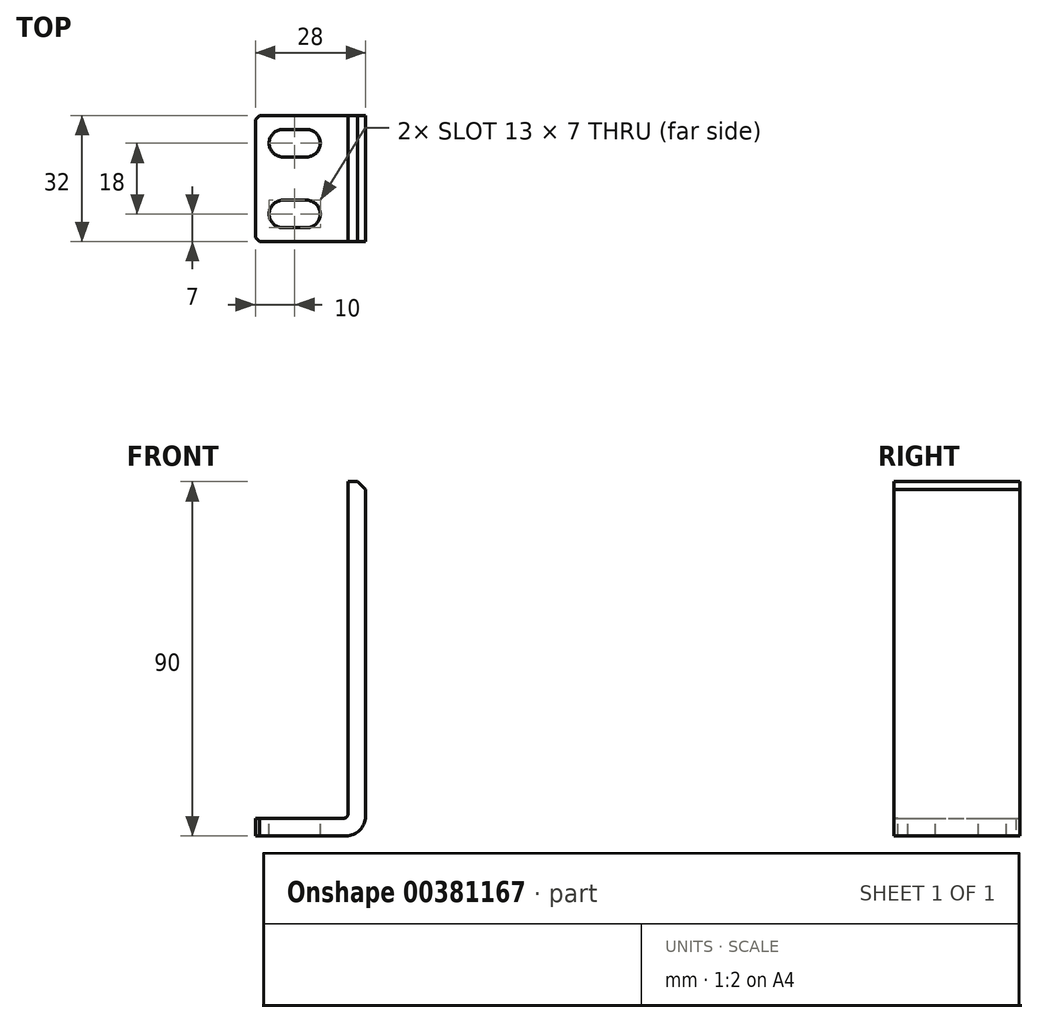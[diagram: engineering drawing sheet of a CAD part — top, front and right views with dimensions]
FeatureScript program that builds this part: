
annotation { "Feature Type Name" : "Feature", "Feature Type Description" : "" }
export const myFeature = defineFeature(function(context is Context, id is Id, definition is map)
    precondition{}
    {
        {
            var Q0;
            Q0=qCreatedBy(makeId("Front.planeOp"),FACE);
            var sketch = newSketch(context, id + "F0", { "sketchPlane" : qUnion([Q0])});
            skLineSegment(sketch, "E0.bottom", {"start": v(0, 90) * mm, "end": v(-4.5, 90) * mm});
            skLineSegment(sketch, "E0.top", {"start": v(0, 0) * mm, "end": v(-28, 0) * mm});
            skLineSegment(sketch, "E0.left", {"start": v(0, 90) * mm, "end": v(0, 0) * mm});
            skLineSegment(sketch, "E0.right", {"start": v(-28, 4.5) * mm, "end": v(-28, 0) * mm});
            skLineSegment(sketch, "E1", {"start": v(-4.5, 90) * mm, "end": v(-4.5, 4.5) * mm});
            skLineSegment(sketch, "E2", {"start": v(-28, 4.5) * mm, "end": v(-4.5, 4.5) * mm});
            skSolve(sketch);
        }
        {
            var Q0;
            Q0=makeQuery(id+"F0.imprint","IMPRINT",FACE,{"disambiguationData":[TD([[makeQuery(id+"F0.imprint","IMPRINT",EDGE,{"derivedFrom":sQuery(id+"F0.wireOp",EDGE,"E0.bottom")}),1.0]])]});
            extrude(context, id + "F1", {"entities" : qUnion([Q0]), "depth" : 32 * mm});
        }
        {
            var Q0;
            Q0=makeQuery(id+"F1.opExtrude","SWEPT_EDGE",EDGE,{"disambiguationData":[OSD([sQuery(id+"F0.wireOp",EDGE,"E1"),sQuery(id+"F0.wireOp",EDGE,"E2")])]});
            fillet(context, id + "F2", {"entities" : qUnion([Q0]), "radius" : 1 * mm, "tangentPropagation" : true, "allowEdgeOverflow" : false});
        }
        {
            var Q0;
            Q0=makeQuery(id+"F1.opExtrude","SWEPT_EDGE",EDGE,{"disambiguationData":[OSD([sQuery(id+"F0.wireOp",EDGE,"E0.top"),sQuery(id+"F0.wireOp",EDGE,"E0.left")])]});
            fillet(context, id + "F3", {"entities" : qUnion([Q0]), "radius" : 5 * mm, "tangentPropagation" : true, "allowEdgeOverflow" : false});
        }
        {
            var Q0;
            Q0=makeQuery(id+"F1.opExtrude","SWEPT_EDGE",EDGE,{"disambiguationData":[OSD([sQuery(id+"F0.wireOp",EDGE,"E0.bottom"),sQuery(id+"F0.wireOp",EDGE,"E0.left")])]});
            chamfer(context, id + "F4", {"entities" : qUnion([Q0]), "width" : 2 * mm, "tangentPropagation" : true});
        }
        {
            var Q0;
            Q0=makeQuery(id+"F1.opExtrude","CAP_EDGE",EDGE,{"disambiguationData":[OSD([sQuery(id+"F0.wireOp",EDGE,"E0.right")])],"isStart":false});
            var Q1;
            Q1=makeQuery(id+"F1.opExtrude","CAP_EDGE",EDGE,{"disambiguationData":[OSD([sQuery(id+"F0.wireOp",EDGE,"E0.right")])],"isStart":true});
            chamfer(context, id + "F5", {"entities" : qUnion([Q0, Q1]), "width" : 1 * mm, "tangentPropagation" : true});
        }
        {
            var Q0;
            Q0=makeQuery(id+"F1.opExtrude","SWEPT_FACE",FACE,{"disambiguationData":[OSD([sQuery(id+"F0.wireOp",EDGE,"E2")])]});
            var sketch = newSketch(context, id + "F6", { "sketchPlane" : qUnion([Q0])});
            skLineSegment(sketch, "E3.bottom", {"start": v(-15, -3.5) * mm, "end": v(-21, -3.5) * mm});
            skLineSegment(sketch, "E3.top", {"start": v(-15, -10.5) * mm, "end": v(-21, -10.5) * mm});
            skPoint(sketch, "E3.middle", {"position": v(-18, -7) * mm});
            skLineSegment(sketch, "E4.bottom", {"start": v(-15, -21.5) * mm, "end": v(-21, -21.5) * mm});
            skLineSegment(sketch, "E4.top", {"start": v(-15, -28.5) * mm, "end": v(-21, -28.5) * mm});
            skPoint(sketch, "E4.middle", {"position": v(-18, -25) * mm});
            skArc(sketch, "E5", {"start": v(-21, -21.5) * mm, "mid": v(-24.5, -25) * mm, "end": v(-21, -28.5) * mm});
            skArc(sketch, "E6", {"start": v(-15, -28.5) * mm, "mid": v(-11.5, -25) * mm, "end": v(-15, -21.5) * mm});
            skArc(sketch, "E7", {"start": v(-21, -3.5) * mm, "mid": v(-24.5, -7) * mm, "end": v(-21, -10.5) * mm});
            skArc(sketch, "E8", {"start": v(-15, -10.5) * mm, "mid": v(-11.5, -7) * mm, "end": v(-15, -3.5) * mm});
            skSolve(sketch);
        }
        {
            var Q0;
            Q0=makeQuery(id+"F6.imprint","IMPRINT",FACE,{"disambiguationData":[TD([[makeQuery(id+"F6.imprint","IMPRINT",EDGE,{"derivedFrom":sQuery(id+"F6.wireOp",EDGE,"E3.bottom")}),1.0]])]});
            var Q1;
            Q1=makeQuery(id+"F6.imprint","IMPRINT",FACE,{"disambiguationData":[TD([[makeQuery(id+"F6.imprint","IMPRINT",EDGE,{"derivedFrom":sQuery(id+"F6.wireOp",EDGE,"E4.bottom")}),1.0]])]});
            extrude(context, id + "F7", {"entities" : qUnion([Q0, Q1]), "operationType" : NewBodyOperationType.REMOVE, "oppositeDirection" : true, "depth" : 4.5 * mm});
        }
    });
